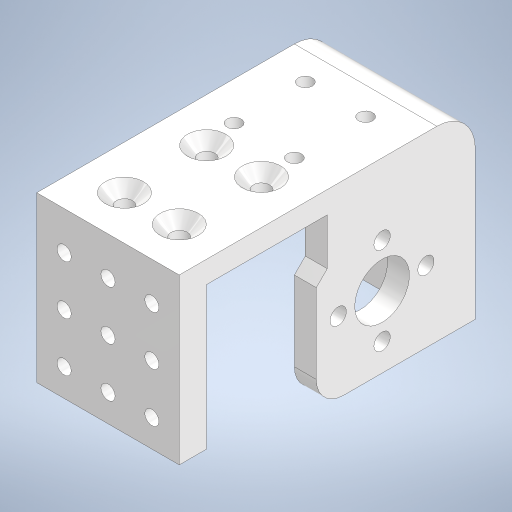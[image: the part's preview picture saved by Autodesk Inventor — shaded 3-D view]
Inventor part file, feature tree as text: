
AUTODESK INVENTOR PART (.ipt)
format: ipt  version: 2024.1 (Build 281209000, 209)  size: 438,272 bytes
history: native  units: mm
features: extrude x11, sketch x11, fillet x3, chamfer x2, mirror x1
ambient origin geometry x8: Origin, YZ Plane, XZ Plane, XY Plane, X Axis, Y Axis, Z Axis, Center Point
bodies: Solid1 (feature_tree)
feature tree (28):
  extrude  "Extrusion1"  Depth=26.0mm
  extrude  "Extrusion2"  Depth=4.0mm
  extrude  "Extrusion3"  Depth=30.0mm TaperAngle=0.0deg
  extrude  "Extrusion4"  Depth=10.0mm
  extrude  "Extrusion6"  TaperAngle=0.0deg  [1 undecoded]
  fillet  "Fillet3"  Radius=3.0mm
  fillet  "Fillet4"  Radius=3.0mm
  fillet  "Fillet5"  Radius=3.0mm
  extrude  "Extrusion7"  Depth=8.0mm
  extrude  "Extrusion8"  Depth=8.0mm
  extrude  "Extrusion9"  Depth=8.0mm
  chamfer  "Chamfer3"  [1 undecoded]
  extrude  "Extrusion10"  Depth=5.0mm
  extrude  "Extrusion11"  Depth=7.0mm
  mirror  "Mirror1"
  extrude  "Extrusion13"  Depth=1.5mm
  chamfer  "Chamfer4"  Distance=30.0mm
  sketch  "Sketch1"  dims[d0=45.0mm d1=26.0mm]
  sketch  "Sketch2"  dims[d2=4.0mm d3=0.0mm d4=4.0mm]
  sketch  "Sketch4"  dims[d5=25.0mm d6=30.0mm d7=0.0mm]
  sketch  "Sketch5"  dims[d8=10.0mm d9=13.0mm]
  sketch  "Sketch9"  dims[d10=13.0mm d11=0.0mm d12=0.0mm d13=3.0mm d14=3.0mm d15=3.0mm]
  sketch  "Sketch10"  dims[d16=3.0mm d17=8.0mm]
  sketch  "Sketch12"  dims[d19=8.0mm d20=8.0mm]
  sketch  "Sketch13"  dims[d21=8.0mm d22=8.0mm]
  sketch  "Sketch14"  dims[d23=8.0mm]
  sketch  "Sketch15"  dims[d24=8.0mm d25=0.0mm d26=0.0mm]
  sketch  "Sketch17"  dims[d39=4.0mm d40=0.0mm d41=5.0mm d42=7.0mm d43=1.5mm d44=30.0mm d45=5.0mm d46=0.0mm d47=2.6mm d48=2.6mm d49=2.6mm d50=2.6mm d51=2.6mm d52=5.0mm d53=5.0mm d54=5.0mm d55=5.0mm d56=7.0mm d57=7.0mm d58=16.0mm d59=5.0mm d60=5.0mm d61=5.0mm d62=10.0mm d63=0.0mm d64=2.6mm d65=16.0mm d66=5.0mm d67=3.0mm d68=3.0mm d69=3.0mm d70=3.0mm d71=10.0mm d72=15.0mm d73=15.0mm d74=8.0mm d75=8.0mm d76=8.0mm d77=8.0mm d78=10.0mm d79=0.0mm d80=0.0mm d81=2.6mm d82=2.6mm d83=2.6mm d84=5.0mm d85=13.0mm d86=13.0mm d87=13.0mm d88=7.0mm d89=16.0mm d90=2.0mm d91=2.0mm d92=45.0deg d93=2.6mm d94=2.6mm d95=2.6mm d96=2.6mm d97=8.0mm d98=8.0mm d99=6.0mm d100=6.0mm d101=8.0mm d102=8.0mm d103=10.0mm d104=10.0mm d105=0.0mm d106=0.0mm d107=2.6mm d108=2.6mm d109=2.6mm d110=2.6mm d111=8.0mm d112=8.0mm d113=7.0mm d114=7.0mm d115=13.0mm d116=13.0mm d117=29.0mm d118=29.0mm d119=10.0mm d120=0.0mm d124=2.0mm d125=8.5mm d126=0.0mm d127=0.0mm d128=2.0mm d129=2.0mm d130=45.0deg]
note: 2 required parameter values undecoded (feature->parameter linkage not recoverable at this tier; creation-order binding heuristic only, values carry confidence <= 0.55)
